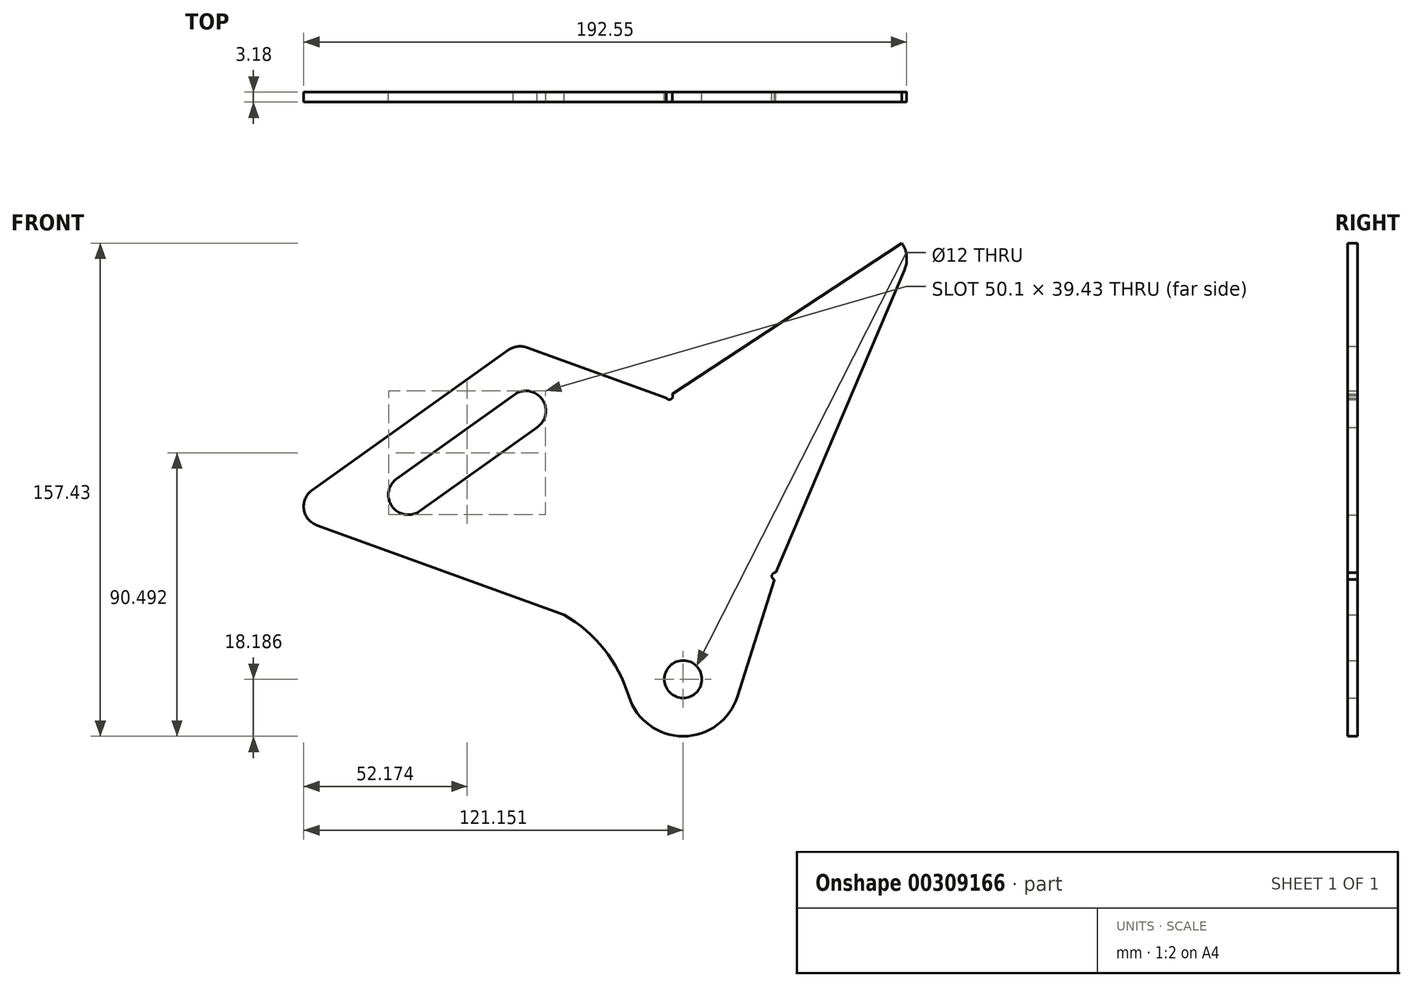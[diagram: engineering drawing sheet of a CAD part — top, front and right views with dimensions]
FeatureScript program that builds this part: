
annotation { "Feature Type Name" : "Feature", "Feature Type Description" : "" }
export const myFeature = defineFeature(function(context is Context, id is Id, definition is map)
    precondition{}
    {
        {
            var Q0;
            Q0=qCreatedBy(makeId("Front.planeOp"),FACE);
            var sketch = newSketch(context, id + "F0", { "sketchPlane" : qUnion([Q0])});
            skLineSegment(sketch, "E0", {"start": v(53.63, 26.52) * mm, "end": v(-19.68, -21.69) * mm});
            skLineSegment(sketch, "E1", {"start": v(12.9, -80.9) * mm, "end": v(1.12, -118.2) * mm});
            skArc(sketch, "E2", {"start": v(-33.56, -118.2) * mm, "mid": v(-16.22, -130.9) * mm, "end": v(1.12, -118.2) * mm});
            skArc(sketch, "E3", {"start": v(-21.59, -22.94) * mm, "mid": v(-20, -23.27) * mm, "end": v(-19.68, -21.69) * mm});
            skArc(sketch, "E4", {"start": v(13.32, -78.67) * mm, "mid": v(12.12, -79.6) * mm, "end": v(12.9, -80.9) * mm});
            skCircle(sketch, "E5", {"center": v(-16.22, -112.72) * mm, "radius": 6 * mm});
            skLineSegment(sketch, "E6", {"start": v(-54.22, -92.14) * mm, "end": v(-96.78, -76.74) * mm});
            skArc(sketch, "E7", {"start": v(-33.56, -118.2) * mm, "mid": v(-41.43, -103.22) * mm, "end": v(-54.22, -92.14) * mm});
            skLineSegment(sketch, "E8", {"start": v(-21.56, -22.98) * mm, "end": v(-66.2, -6.82) * mm});
            skLineSegment(sketch, "E9", {"start": v(-96.78, -76.74) * mm, "end": v(-133.18, -63.56) * mm});
            skLineSegment(sketch, "E10", {"start": v(-134.71, -52.42) * mm, "end": v(-72.05, -7.63) * mm});
            skPoint(sketch, "E11.visualSharp", {"position": v(-144.54, -59.45) * mm});
            skArc(sketch, "E11.filletArc", {"start": v(-134.71, -52.42) * mm, "mid": v(-137.31, -58.45) * mm, "end": v(-133.18, -63.56) * mm});
            skPoint(sketch, "E12.visualSharp", {"position": v(-69.33, -5.69) * mm});
            skArc(sketch, "E12.filletArc", {"start": v(-66.2, -6.82) * mm, "mid": v(-69.22, -6.5) * mm, "end": v(-72.05, -7.63) * mm});
            skArc(sketch, "E13", {"start": v(-107.67, -48.7) * mm, "mid": v(-109.15, -57.56) * mm, "end": v(-100.29, -59.04) * mm});
            skArc(sketch, "E14", {"start": v(-62.92, -32.32) * mm, "mid": v(-61.3, -23.22) * mm, "end": v(-70.48, -22.14) * mm});
            skLineSegment(sketch, "E15", {"start": v(-70.48, -22.14) * mm, "end": v(-107.67, -48.7) * mm});
            skLineSegment(sketch, "E16", {"start": v(-62.92, -32.32) * mm, "end": v(-100.29, -59.04) * mm});
            skLineSegment(sketch, "E17", {"start": v(53.63, 26.52) * mm, "end": v(53.72, 26.38) * mm});
            skLineSegment(sketch, "E18", {"start": v(54.47, 18.01) * mm, "end": v(13.32, -78.67) * mm});
            skPoint(sketch, "E19.visualSharp", {"position": v(56.34, 22.4) * mm});
            skArc(sketch, "E19.filletArc", {"start": v(54.47, 18.01) * mm, "mid": v(55.14, 22.3) * mm, "end": v(53.72, 26.38) * mm});
            skSolve(sketch);
        }
        {
            var Q0;
            Q0 = qSketchRegion(id + "F0", true);
            extrude(context, id + "F1", {"entities" : qUnion([Q0]), "depth" : 3.17 * mm});
        }
    });
